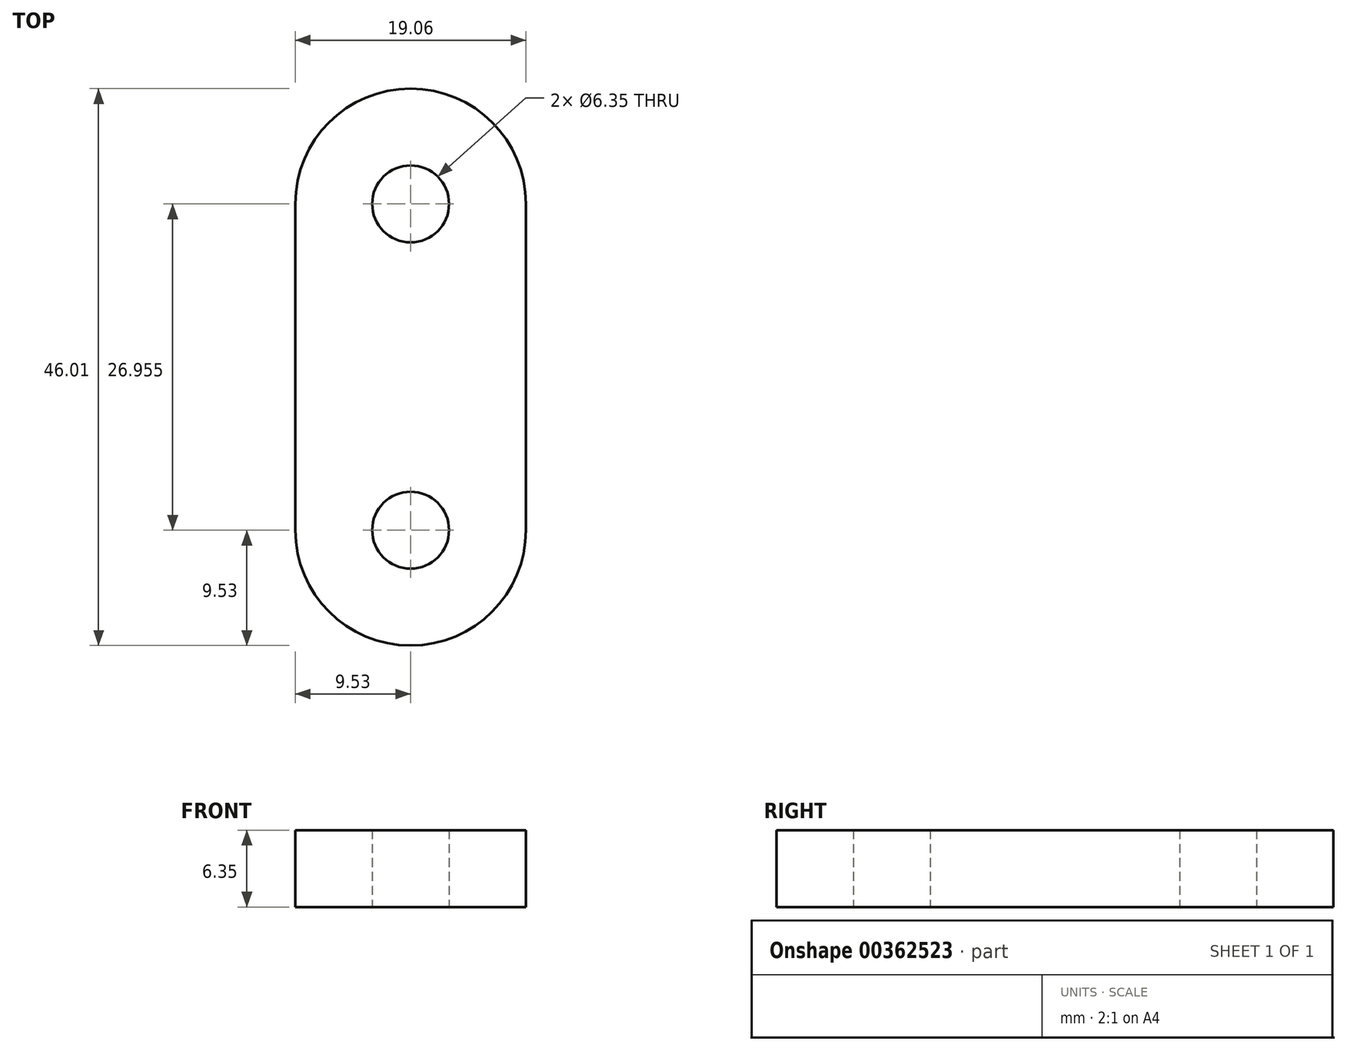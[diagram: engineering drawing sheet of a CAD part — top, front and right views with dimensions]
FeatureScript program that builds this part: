
annotation { "Feature Type Name" : "Feature", "Feature Type Description" : "" }
export const myFeature = defineFeature(function(context is Context, id is Id, definition is map)
    precondition{}
    {
        {
            var Q0;
            Q0=qCreatedBy(makeId("Top.planeOp"),FACE);
            var sketch = newSketch(context, id + "F0", { "sketchPlane" : qUnion([Q0])});
            skLineSegment(sketch, "E0", {"start": v(0, 0) * mm, "end": v(0, 26.96) * mm});
            skCircle(sketch, "E1", {"center": v(0, 26.96) * mm, "radius": 3.17 * mm});
            skCircle(sketch, "E2", {"center": v(0, 0) * mm, "radius": 3.17 * mm});
            skCircle(sketch, "E3", {"center": v(0, 0) * mm, "radius": 9.53 * mm});
            skCircle(sketch, "E4", {"center": v(0, 26.96) * mm, "radius": 9.53 * mm});
            skLineSegment(sketch, "E5", {"start": v(-9.53, 26.96) * mm, "end": v(-9.53, 0) * mm});
            skLineSegment(sketch, "E6", {"start": v(0, 26.96) * mm, "end": v(9.53, 26.96) * mm});
            skLineSegment(sketch, "E7", {"start": v(9.53, 26.96) * mm, "end": v(9.53, 0) * mm});
            skSolve(sketch);
        }
        {
            var Q0;
            Q0 = qSketchRegion(id + "F0", true);
            extrude(context, id + "F1", {"entities" : qUnion([Q0]), "depth" : 6.35 * mm});
        }
    });
